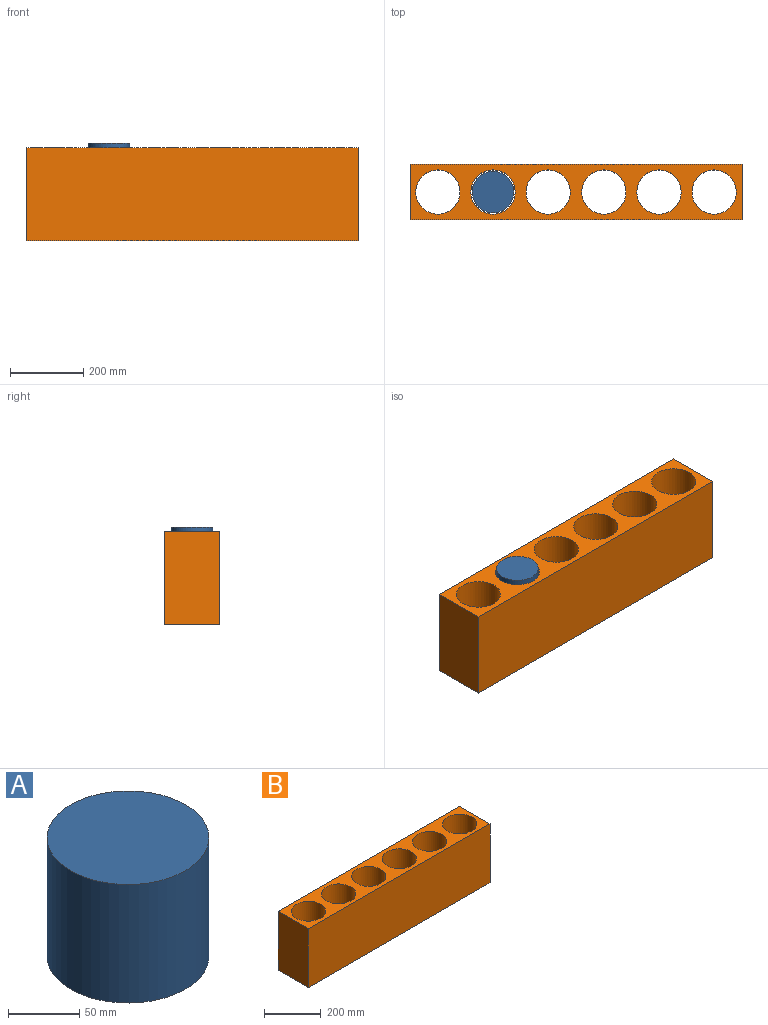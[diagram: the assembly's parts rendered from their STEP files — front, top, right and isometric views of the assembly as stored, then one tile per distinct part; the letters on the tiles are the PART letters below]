
ASSEMBLY  parts=2 mates=1
PART A: 3 faces, bbox 113.4x113.4x101.6 mm
  f0: cylinder r=56.72mm len=113.45mm, axis (0,0,-1), area 36210.1mm2, adj f1,f2
  f1: plane 113.45x113.45mm, normal (0,0,1), area 10108mm2, adj f0
  f2: plane 113.45x113.45mm, normal (0,0,-1), area 10108mm2, adj f0
PART B: 12 faces, bbox 904.8x150.8x254 mm
  f0: plane 904.84x254mm, normal (0,1,0), area 229828.6mm2, adj f2,f3,f5,f9
  f1: plane 904.84x254mm, normal (0,-1,0), area 229828.6mm2, adj f2,f3,f5,f9
  f2: plane 904.84x150.78mm, normal (0,0,1), area 67837.2mm2, adj f0,f1,f4,f5,f6,f7,f8,f9
  f3: plane 904.84x150.78mm, normal (0,0,-1), area 67837.2mm2, adj f0,f1,f4,f5,f6,f7,f8,f9
  f4: cylinder r=60.32mm len=254mm, axis (0,0,1), area 96274.4mm2, adj f2,f3
  f5: plane 254x150.78mm, normal (-1,0,0), area 38298.5mm2, adj f0,f1,f2,f3
  f6: cylinder r=60.32mm len=254mm, axis (0,0,1), area 96274.4mm2, adj f2,f3
  f7: cylinder r=60.32mm len=254mm, axis (0,0,1), area 96274.4mm2, adj f2,f3
  f8: cylinder r=60.32mm len=254mm, axis (0,0,1), area 96274.4mm2, adj f2,f3
  f9: plane 254x150.78mm, normal (1,0,0), area 38298.5mm2, adj f0,f1,f2,f3
  f10: cylinder r=60.32mm len=254mm, axis (0,0,1), area 96274.4mm2, adj f2,f3
  f11: cylinder r=60.32mm len=254mm, axis (0,0,1), area 96274.4mm2, adj f2,f3
PLACE A t=(79.21,776.83,164.37)mm
PLACE B t=(79.21,776.83,0)mm
MATE cylindrical A.f0 <-> B.f4  axis (0,0,1) through (79.21,776.83,265.97)mm
